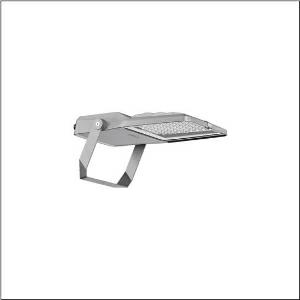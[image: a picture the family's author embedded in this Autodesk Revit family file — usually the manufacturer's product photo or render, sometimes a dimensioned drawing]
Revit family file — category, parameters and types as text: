
# Revit family: floodlight_fl_21_iq_mini___pl61_5xa7771b4c1a_7efd
name_source: partatom
category: Lighting Fixtures
units: mm (PartAtom-declared; Revit-internal decimal feet)

## family parameters
Cut with Voids When Loaded = No
Host = Face
Light Source = No
Part Type = Normal
Room Calculation Point = No
Round Connector Dimension = Use Diameter
Shared = No

## types (1)
- --- (1 x LED, 6370 lm, 45.5 W, 4000K)
    Apparent Load = 46 VA
    CIE Flux Codes = 33 65 98 100 100
    Color Rendering = 70
    Color Temperature = 4000K
    Default Elevation = 1800 mm
    Description = Floodlight FL 21 iQ mini, floodlight, primary light control with lens, of PMMA, primary optical cover: protective disc, of toughened safety glass, transparent, light distribution: PL61, light emission: direct distribution, installation type: surface-mounted, LED, High Power LED, rated luminous flux: 6.370lm, luminous efficacy: 140lm/W, light colour: 740, colour temperature: 4000K, control gear: iQ Comfort/DALI, control: Auto-Match, Temp-Guard, Lumen-Switch, Night-Set, Smart-Wire, Light-Fading, Desk-Remote (wireless, voltage-free reading and setting of iQ features in the workshop via application-optimized NFC function/RFID function), optimised constant luminous flux control (CLO 2.0), with terminal, 6-pole, mains connection: 220..240V, AC, 50/60Hz, start of lifetime: 46W, end of service life: 48W, reduction: 22W, luminaire housing, of diecast aluminium, powder-coated, Siteco® metallic grey (DB 702S), corrosivity category C5 mid according to DIN EN ISO 12944, suitable for swimming pools, chlorine-resistant, sealing non-destructively replaceable, mounting bracket, of steel, galvanised, powder-coated, Siteco® metallic grey (DB 702S), protection rating (complete): IP66, insulation class (complete): insulation class II (safety insulation), certification: CE, ENEC, VDE, protection symbol: D, impact resistance: IK08, permissible operating ambient temperature: -40..+40°C, permissible operating ambient temperature for outdoor applications: -40..+50°C, standard: DIN EN 12944, LABS conformity tested according to VDMA 24364:2018-05, packaging unit: 1 piece

Light Distribution: PL61
    Height = 70 mm
    Lamp = 1 x LED
    Lamp Light Flux = 6370 lm
    Lamp Power = 45.5 W
    Lamp count = 1
    Length = 485 mm
    Luminous efficacy = 140 lm/W
    Manufacturer = Siteco
    ModVariant = No
    Model = 5XA7771B4C1A
    Mounting Place = Wall
    Mounting Type = Surface mounted
    Number of Poles = 1
    OnlyDefault = Yes
    Power Factor = 1
    Product Name = Floodlight FL 21 iQ mini | PL61
    Product group = floodlight | wall mounted
    ProductGroupID = 2001
    Protection Class = Protection class II
    Protection Degree = IP 66
    RLX_Detail_Level = 1
    RLX_Emergency_Light_Flux = 0 lm
    RLX_Emergency_Type = 0
    RLX_Emergency_Type_DB = No
    RlxData = <blob elided: 96333 chars, md5=075b0b65>
    Socket = socket
    Standby Power = 0 W
    System Light Flux = 6370 lm
    System Power = 46 W
    Type Comments = factory setting: luminous flux: 100 % | dim-lin: 254 | 463 mA
    Type Image = l_1006845.jpg
    URL = http://relux.com
    VarID = @adj_173800
    Voltage = 0 V
    Weight = 0.00 kg
    Width = 337 mm

## geometry (parser evidence)
native form markers: Blend x4, Sweep x13
no freeform markers — native parametric forms only
